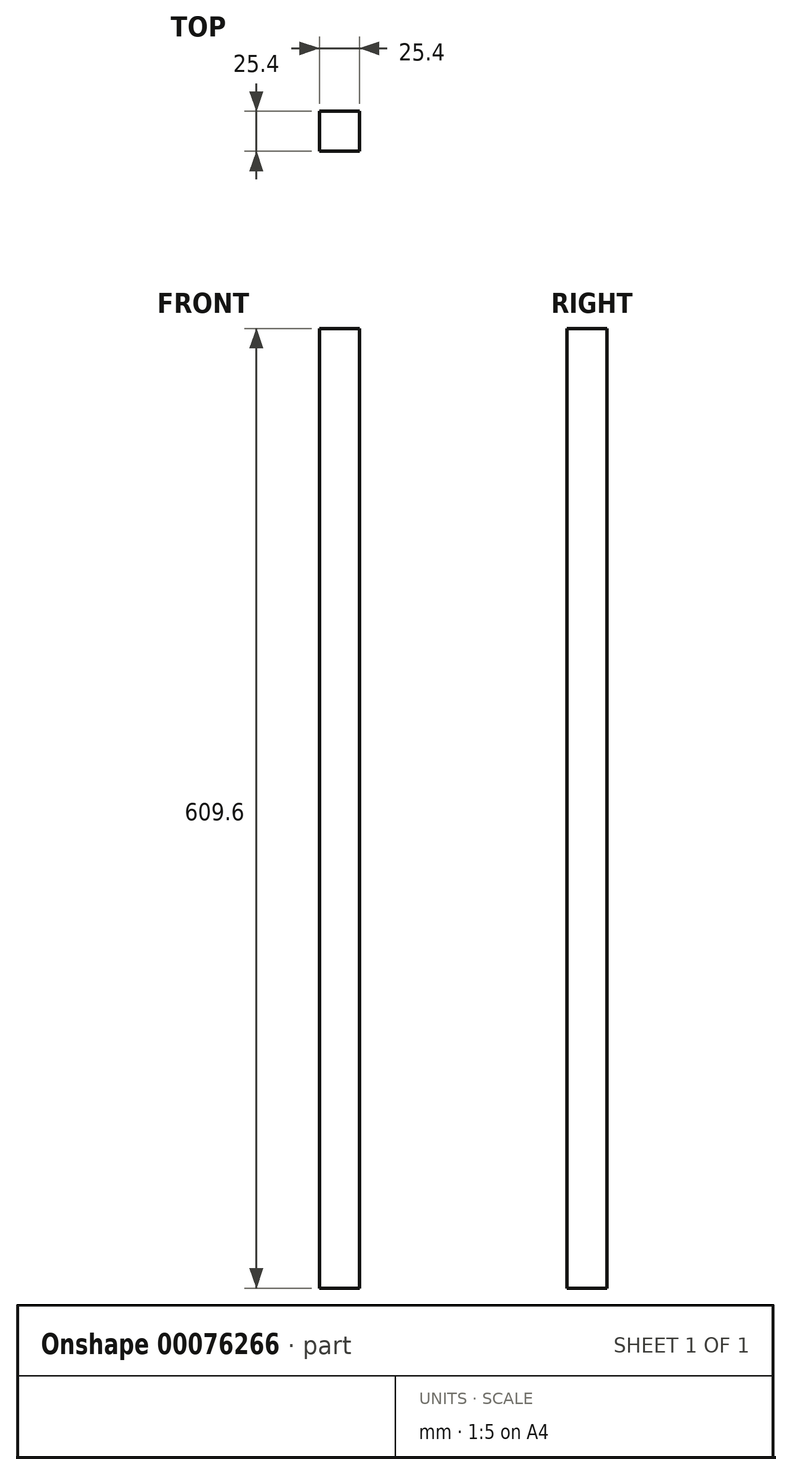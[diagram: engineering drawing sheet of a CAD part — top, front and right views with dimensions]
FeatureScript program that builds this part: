
annotation { "Feature Type Name" : "Feature", "Feature Type Description" : "" }
export const myFeature = defineFeature(function(context is Context, id is Id, definition is map)
    precondition{}
    {
        {
            var Q0;
            Q0=qCreatedBy(makeId("Top.planeOp"),FACE);
            var sketch = newSketch(context, id + "F0", { "sketchPlane" : qUnion([Q0])});
            skLineSegment(sketch, "E0.bottom", {"start": v(12.53, 12.08) * mm, "end": v(-12.87, 12.08) * mm});
            skLineSegment(sketch, "E0.top", {"start": v(12.53, -13.32) * mm, "end": v(-12.87, -13.32) * mm});
            skLineSegment(sketch, "E0.left", {"start": v(12.53, 12.08) * mm, "end": v(12.53, -13.32) * mm});
            skLineSegment(sketch, "E0.right", {"start": v(-12.87, 12.08) * mm, "end": v(-12.87, -13.32) * mm});
            skPoint(sketch, "E0.middle", {"position": v(-0.17, -0.62) * mm});
            skSolve(sketch);
        }
        {
            var Q0;
            Q0 = qSketchRegion(id + "F0", true);
            extrude(context, id + "F1", {"entities" : qUnion([Q0]), "depth" : 609.6 * mm});
        }
    });
